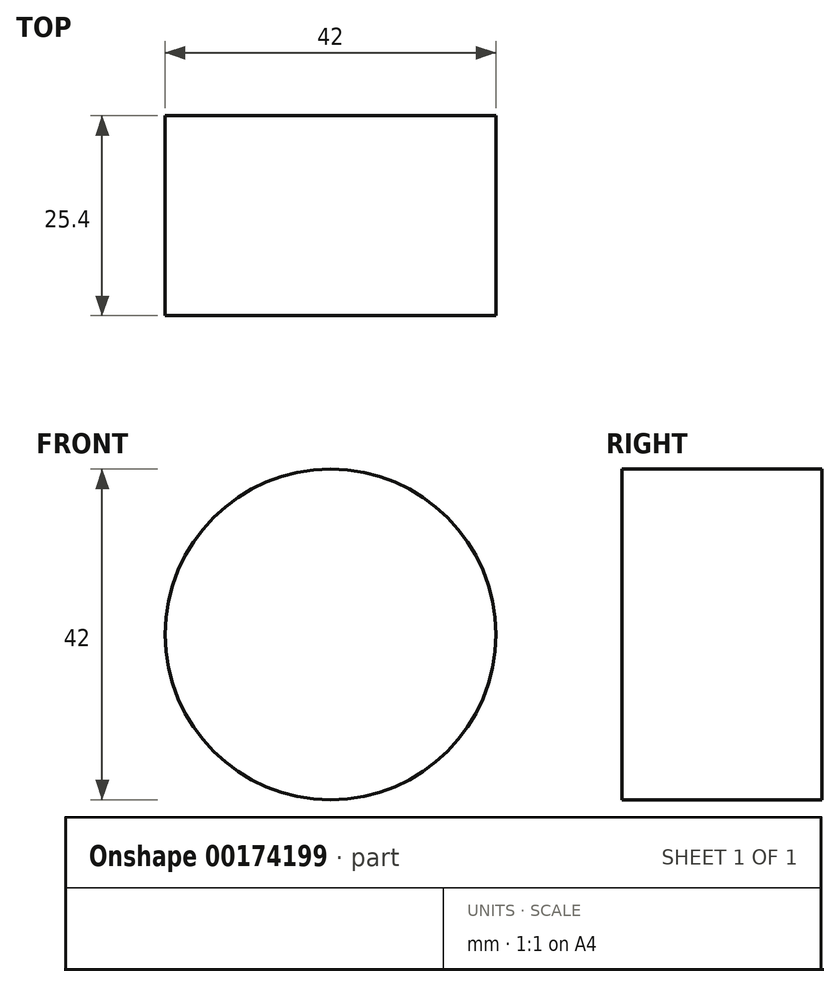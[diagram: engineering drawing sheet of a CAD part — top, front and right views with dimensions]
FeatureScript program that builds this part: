
annotation { "Feature Type Name" : "Feature", "Feature Type Description" : "" }
export const myFeature = defineFeature(function(context is Context, id is Id, definition is map)
    precondition{}
    {
        {
            var Q0;
            Q0=qCreatedBy(makeId("Front.planeOp"),FACE);
            var sketch = newSketch(context, id + "F0", { "sketchPlane" : qUnion([Q0])});
            skCircle(sketch, "E0", {"center": v(0, 0) * mm, "radius": 21 * mm});
            skSolve(sketch);
        }
        {
            var Q0;
            Q0 = qSketchRegion(id + "F0", true);
            extrude(context, id + "F1", {"entities" : qUnion([Q0]), "depth" : 25.4 * mm});
        }
    });
